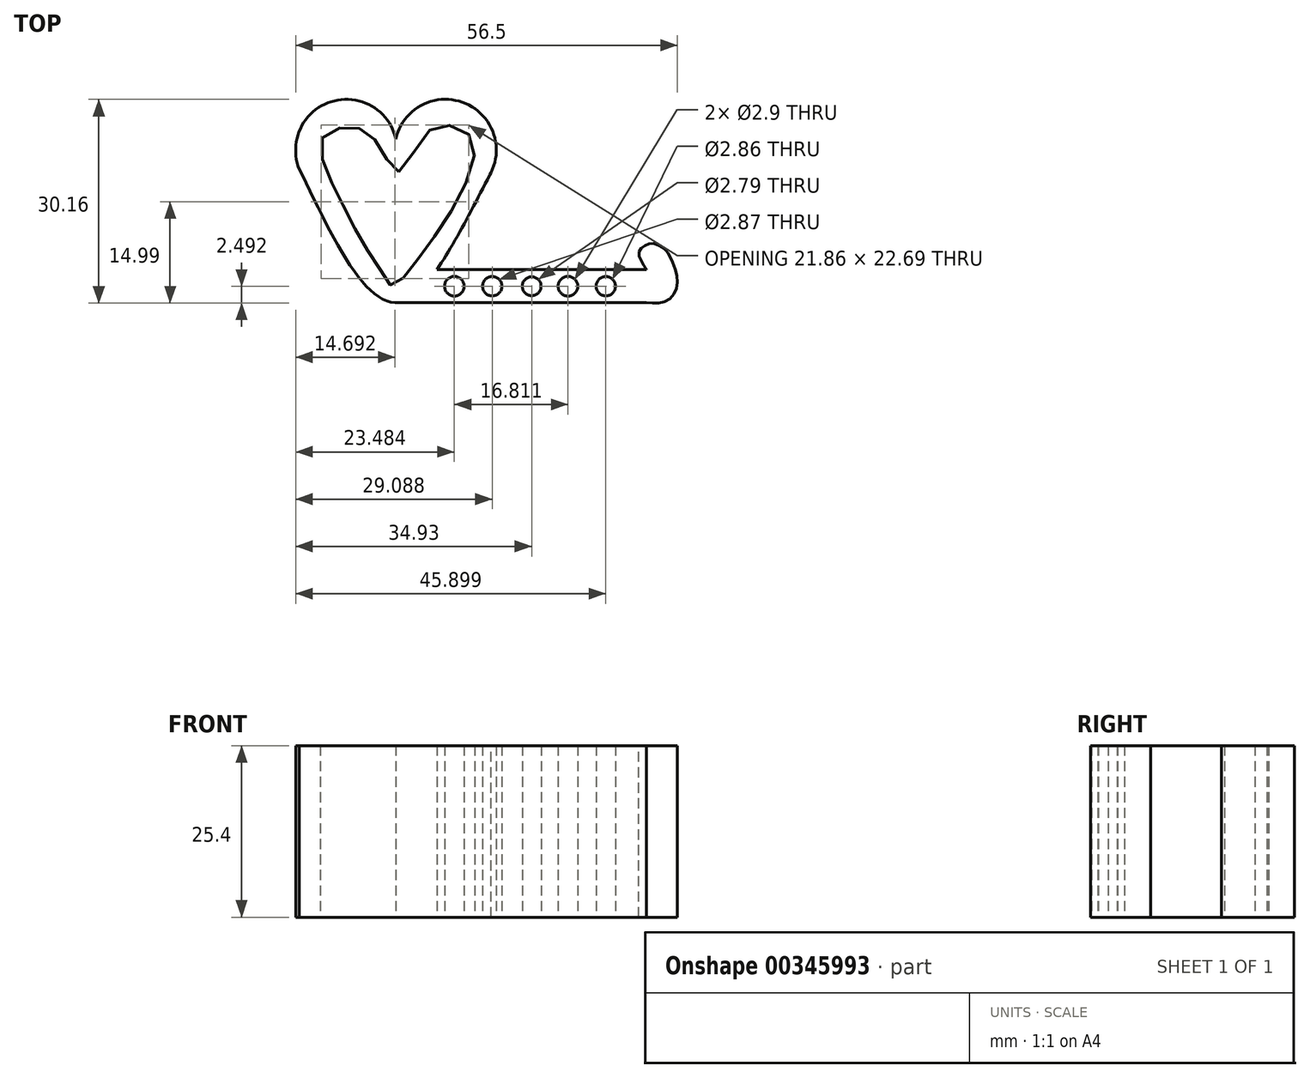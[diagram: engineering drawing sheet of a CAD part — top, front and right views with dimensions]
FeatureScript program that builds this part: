
annotation { "Feature Type Name" : "Feature", "Feature Type Description" : "" }
export const myFeature = defineFeature(function(context is Context, id is Id, definition is map)
    precondition{}
    {
        {
            var Q0;
            Q0=qCreatedBy(makeId("Top.planeOp"),FACE);
            var sketch = newSketch(context, id + "F0", { "sketchPlane" : qUnion([Q0])});
            skArc(sketch, "E0", {"start": v(-18.7, 20.83) * mm, "mid": v(-28.71, 26.2) * mm, "end": v(-32.57, 15.5) * mm});
            skArc(sketch, "E1", {"start": v(-4.79, 15.52) * mm, "mid": v(-8.67, 26.2) * mm, "end": v(-18.7, 20.83) * mm});
            skFitSpline(sketch, "E2", {"points": [v(-32.97, 16.33) * mm, v(-18.87, -3.36) * mm, v(-4.62, 15.85) * mm], "startDerivative": vector(27.4, -56.67) * mm, "endDerivative": vector(29.32, 55.69) * mm});
            skLineSegment(sketch, "E3", {"start": v(-12.64, 1.52) * mm, "end": v(18.39, 1.52) * mm});
            skLineSegment(sketch, "E4", {"start": v(-18.87, -3.36) * mm, "end": v(18.39, -3.36) * mm});
            skCircle(sketch, "E5", {"center": v(-10.05, -0.97) * mm, "radius": 1.45 * mm});
            skCircle(sketch, "E6", {"center": v(-4.44, -0.97) * mm, "radius": 1.44 * mm});
            skCircle(sketch, "E7", {"center": v(1.4, -0.97) * mm, "radius": 1.4 * mm});
            skCircle(sketch, "E8", {"center": v(6.76, -0.97) * mm, "radius": 1.45 * mm});
            skCircle(sketch, "E9", {"center": v(12.37, -0.97) * mm, "radius": 1.43 * mm});
            skFitSpline(sketch, "E10.trimOffspring", {"points": [v(18.24, 1.79) * mm, v(15.67, 5.18) * mm, v(18.87, 0.88) * mm, v(18.87, 0.88) * mm], "startDerivative": vector(0.42, -0.62) * mm, "endDerivative": vector(0.04, 0.14) * mm});
            skFitSpline(sketch, "E11", {"points": [v(18.39, 1.52) * mm, v(17.66, 2.68) * mm, v(17.28, 4.16) * mm, v(18.24, 5.07) * mm, v(19.53, 5.35) * mm, v(21.1, 4.46) * mm, v(21.57, 3.93) * mm, v(22.63, 1.52) * mm, v(22.79, -1.5) * mm, v(20.99, -3.3) * mm, v(18.39, -3.36) * mm], "startDerivative": vector(-8.96, 12.48) * mm, "endDerivative": vector(-21.65, 2.09) * mm});
            skFitSpline(sketch, "E12", {"points": [v(-18.57, 18) * mm, v(-20.67, 21.88) * mm, v(-23.01, 24.3) * mm, v(-25.35, 25.19) * mm, v(-28.67, 24.79) * mm, v(-31.01, 22.36) * mm, v(-31.74, 20.02) * mm, v(-31.01, 16.95) * mm, v(-27.62, 9.6) * mm, v(-24.38, 3.05) * mm, v(-20.75, -1.4) * mm, v(-19.3, -2.2) * mm, v(-17.2, -1.56) * mm, v(-14.12, 1.84) * mm, v(-10.89, 7) * mm, v(-6.12, 16.06) * mm, v(-6.2, 21.63) * mm, v(-8.7, 24.62) * mm, v(-12.9, 25.1) * mm, v(-15.98, 23.09) * mm, v(-17.35, 20.26) * mm, v(-18.57, 18) * mm]});
            skFitSpline(sketch, "E13", {"points": [v(-18.24, 15.98) * mm, v(-20.34, 18.4) * mm, v(-22.93, 21.8) * mm, v(-26.16, 22.6) * mm, v(-29.56, 20.99) * mm, v(-29.07, 16.38) * mm, v(-26.49, 10.97) * mm, v(-23.58, 5.39) * mm, v(-20.9, 1.27) * mm, v(-19.21, -0.91) * mm, v(-16.87, 1.19) * mm, v(-12.83, 6.6) * mm, v(-8.3, 14.36) * mm, v(-7.33, 20.74) * mm, v(-10.8, 22.85) * mm, v(-14.6, 21.23) * mm, v(-18.24, 15.98) * mm]});
            skSolve(sketch);
        }
        {
            var Q0;
            Q0=makeQuery(id+"F0.imprint","IMPRINT",FACE,{"disambiguationData":[TD([[makeQuery(id+"F0.imprint","IMPRINT",EDGE,{"derivedFrom":sQuery(id+"F0.wireOp",EDGE,"E12")}),-1.0]])]});
            var Q1;
            {var subQ0=sQuery(id+"F0.wireOp",EDGE,"E3");Q1=makeQuery(id+"F0.imprint","IMPRINT",FACE,{"disambiguationData":[TD([[makeQuery(id+"F0.imprint","IMPRINT",EDGE,{"derivedFrom":subQ0}),-1.0]])]});}
            var Q2;
            Q2=makeQuery(id+"F0.imprint","IMPRINT",FACE,{"disambiguationData":[TD([[makeQuery(id+"F0.imprint","IMPRINT",EDGE,{"derivedFrom":sQuery(id+"F0.wireOp",EDGE,"E12")}),1.0]])]});
            extrude(context, id + "F1", {"entities" : qUnion([Q0, Q1, Q2]), "depth" : 25.4 * mm});
        }
    });
